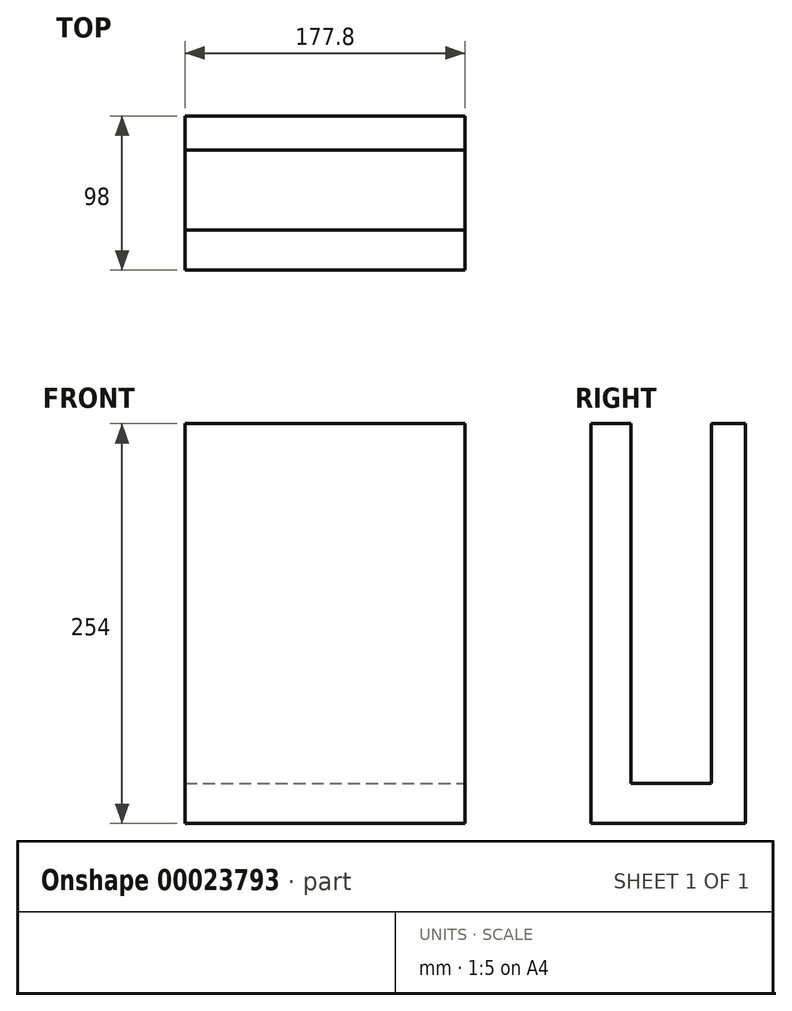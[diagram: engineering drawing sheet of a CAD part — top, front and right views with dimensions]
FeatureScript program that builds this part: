
annotation { "Feature Type Name" : "Feature", "Feature Type Description" : "" }
export const myFeature = defineFeature(function(context is Context, id is Id, definition is map)
    precondition{}
    {
        {
            var Q0;
            Q0=qCreatedBy(makeId("Front.planeOp"),FACE);
            var sketch = newSketch(context, id + "F0", { "sketchPlane" : qUnion([Q0])});
            skLineSegment(sketch, "E0.bottom", {"start": v(-66.18, 121.93) * mm, "end": v(111.62, 121.93) * mm});
            skLineSegment(sketch, "E0.top", {"start": v(-66.18, -132.07) * mm, "end": v(111.62, -132.07) * mm});
            skLineSegment(sketch, "E0.left", {"start": v(-66.18, 121.93) * mm, "end": v(-66.18, -132.07) * mm});
            skLineSegment(sketch, "E0.right", {"start": v(111.62, 121.93) * mm, "end": v(111.62, -132.07) * mm});
            skLineSegment(sketch, "E1", {"start": v(0, 0) * mm, "end": v(0, 158.9) * mm, "construction": true});
            skLineSegment(sketch, "E2", {"start": v(0, 158.9) * mm, "end": v(0, -158.9) * mm, "construction": true});
            skLineSegment(sketch, "E3", {"start": v(0, -158.9) * mm, "end": v(0, 0) * mm, "construction": true});
            skLineSegment(sketch, "E4", {"start": v(288.58, 0) * mm, "end": v(-393.52, 0) * mm, "construction": true});
            skSolve(sketch);
        }
        {
            var Q0;
            Q0 = qSketchRegion(id + "F0", true);
            extrude(context, id + "F1", {"entities" : qUnion([Q0]), "depth" : 25.4 * mm});
        }
        {
            var Q0;
            Q0=makeQuery(id+"F1.opExtrude","SWEPT_FACE",FACE,{"disambiguationData":[OSD([sQuery(id+"F0.wireOp",EDGE,"E0.top")])]});
            var sketch = newSketch(context, id + "F2", { "sketchPlane" : qUnion([Q0])});
            skLineSegment(sketch, "E5.bottom", {"start": v(-66.18, 25.4) * mm, "end": v(111.62, 25.4) * mm});
            skLineSegment(sketch, "E5.top", {"start": v(-66.18, -72.6) * mm, "end": v(111.62, -72.6) * mm});
            skLineSegment(sketch, "E5.left", {"start": v(-66.18, 25.4) * mm, "end": v(-66.18, -72.6) * mm});
            skLineSegment(sketch, "E5.right", {"start": v(111.62, 25.4) * mm, "end": v(111.62, -72.6) * mm});
            skLineSegment(sketch, "E6", {"start": v(-66.18, -50.98) * mm, "end": v(111.62, -50.98) * mm});
            skSolve(sketch);
        }
        {
            var Q0;
            {var subQ2=sQuery(id+"F2.wireOp",EDGE,"E5.top");Q0=makeQuery(id+"F2.imprint","IMPRINT",FACE,{"disambiguationData":[TD([[makeQuery(id+"F2.imprint","IMPRINT",EDGE,{"derivedFrom":subQ2}),1.0]])]});}
            extrude(context, id + "F3", {"entities" : qUnion([Q0]), "oppositeDirection" : true, "depth" : 254 * mm});
        }
        {
            var Q0;
            {var subQ1=sQuery(id+"F2.wireOp",EDGE,"E6");Q0=makeQuery(id+"F2.imprint","IMPRINT",FACE,{"disambiguationData":[TD([[makeQuery(id+"F2.imprint","IMPRINT",EDGE,{"derivedFrom":subQ1}),1.0]])]});}
            extrude(context, id + "F4", {"entities" : qUnion([Q0]), "operationType" : NewBodyOperationType.ADD, "oppositeDirection" : true, "depth" : 25.4 * mm});
        }
    });
